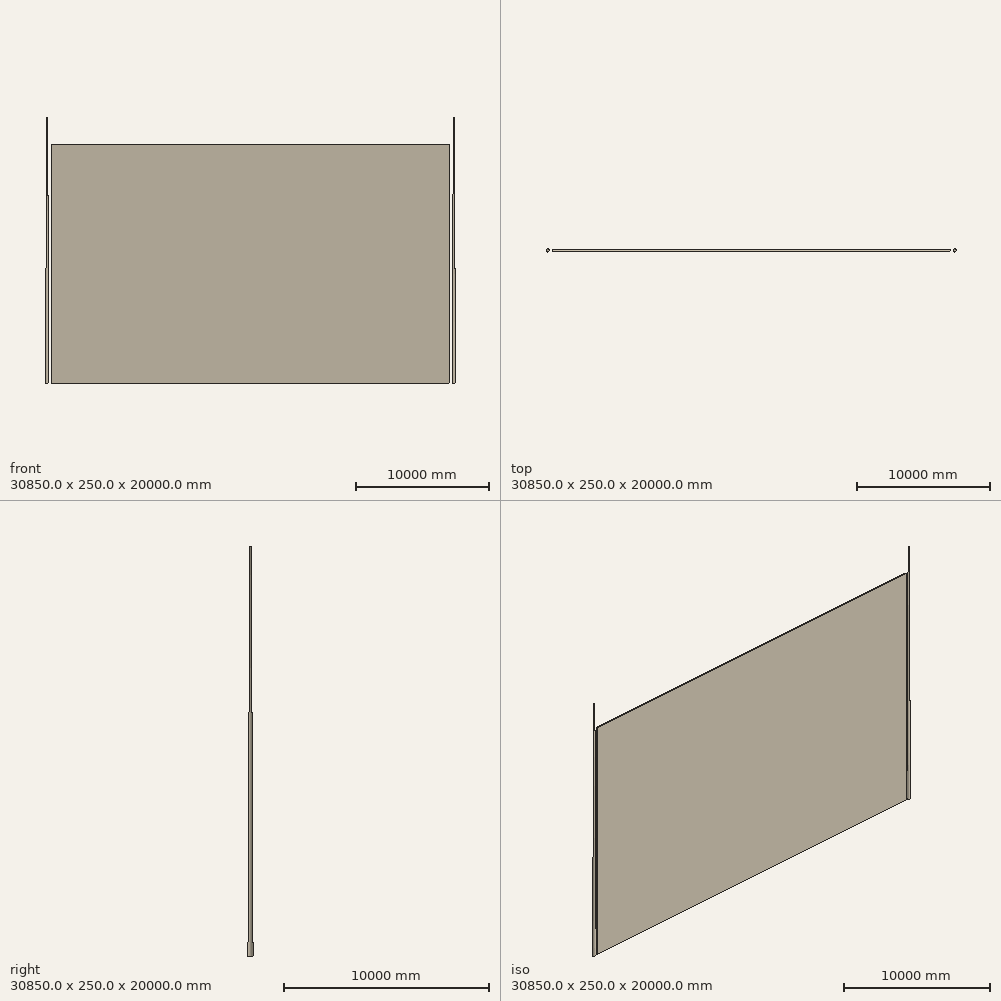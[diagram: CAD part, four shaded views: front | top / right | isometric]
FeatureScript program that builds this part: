
annotation { "Feature Type Name" : "Feature", "Feature Type Description" : "" }
export const myFeature = defineFeature(function(context is Context, id is Id, definition is map)
    precondition{}
    {
        {
            var Q0;
            Q0=qCreatedBy(makeId("Top.planeOp"),FACE);
            var sketch = newSketch(context, id + "F0", { "sketchPlane" : qUnion([Q0])});
            skCircle(sketch, "E0", {"center": v(-15300, 0) * mm, "radius": 125 * mm});
            skCircle(sketch, "E1", {"center": v(15300, 0) * mm, "radius": 125 * mm});
            skLineSegment(sketch, "E2.rect.bottom", {"start": v(-15000, 50) * mm, "end": v(15000, 50) * mm});
            skLineSegment(sketch, "E2.rect.top", {"start": v(-15000, -50) * mm, "end": v(15000, -50) * mm});
            skLineSegment(sketch, "E2.rect.left", {"start": v(-15000, 50) * mm, "end": v(-15000, -50) * mm});
            skLineSegment(sketch, "E2.rect.right", {"start": v(15000, 50) * mm, "end": v(15000, -50) * mm});
            skPoint(sketch, "E2.rect.middle", {"position": v(0, 0) * mm});
            skSolve(sketch);
        }
        {
            var Q0;
            Q0=makeQuery(id+"F0.imprint","IMPRINT",FACE,{"disambiguationData":[TD([[makeQuery(id+"F0.imprint","IMPRINT",EDGE,{"derivedFrom":sQuery(id+"F0.wireOp",EDGE,"E1")}),1.0]])]});
            var Q1;
            Q1=makeQuery(id+"F0.imprint","IMPRINT",FACE,{"disambiguationData":[TD([[makeQuery(id+"F0.imprint","IMPRINT",EDGE,{"derivedFrom":sQuery(id+"F0.wireOp",EDGE,"E0")}),1.0]])]});
            extrude(context, id + "F1", {"entities" : qUnion([Q0, Q1]), "depth" : 20000 * mm, "hasDraft" : true, "draftAngle" : .25 * degree, "draftPullDirection" : true});
        }
        {
            var Q0;
            Q0=makeQuery(id+"F0.imprint","IMPRINT",FACE,{"disambiguationData":[TD([[makeQuery(id+"F0.imprint","IMPRINT",EDGE,{"derivedFrom":sQuery(id+"F0.wireOp",EDGE,"E2.rect.bottom")}),-1.0]])]});
            extrude(context, id + "F2", {"entities" : qUnion([Q0]), "depth" : 18000 * mm});
        }
    });
